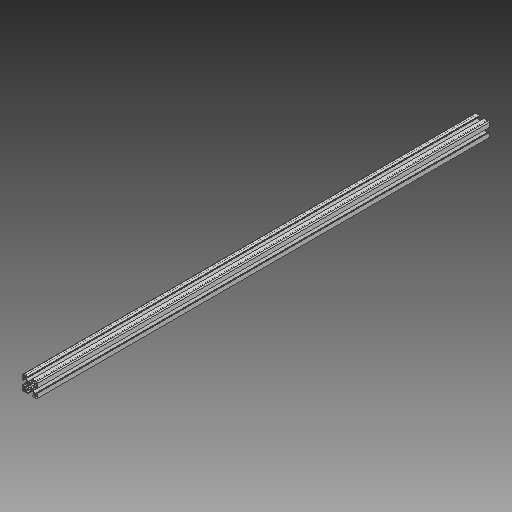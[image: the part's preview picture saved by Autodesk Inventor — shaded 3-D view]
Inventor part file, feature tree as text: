
AUTODESK INVENTOR PART (.ipt)
format: ipt  version: 2018 (Build 220112000, 112)  size: 276,992 bytes
history: native  units: mm
features: other x2, extrude x1, sketch x1, reference x1
ambient origin geometry x8: Origin, YZ Plane, XZ Plane, XY Plane, X Axis, Y Axis, Z Axis, Center Point
bodies: Solid1 (feature_tree)
feature tree (5):
  extrude  "Extrusion1"  [1 undecoded]
  sketch  "Sketch1"  dims[d0=900.0mm d1=0.0mm]
  reference  "Reference1"
  other  "<userpath>\OneDrive\Inventor\Beast 3D Printer\Assembly3.iam"
  other  "Assembly3.iam"
note: 1 required parameter value undecoded (feature->parameter linkage not recoverable at this tier; creation-order binding heuristic only, values carry confidence <= 0.55)
